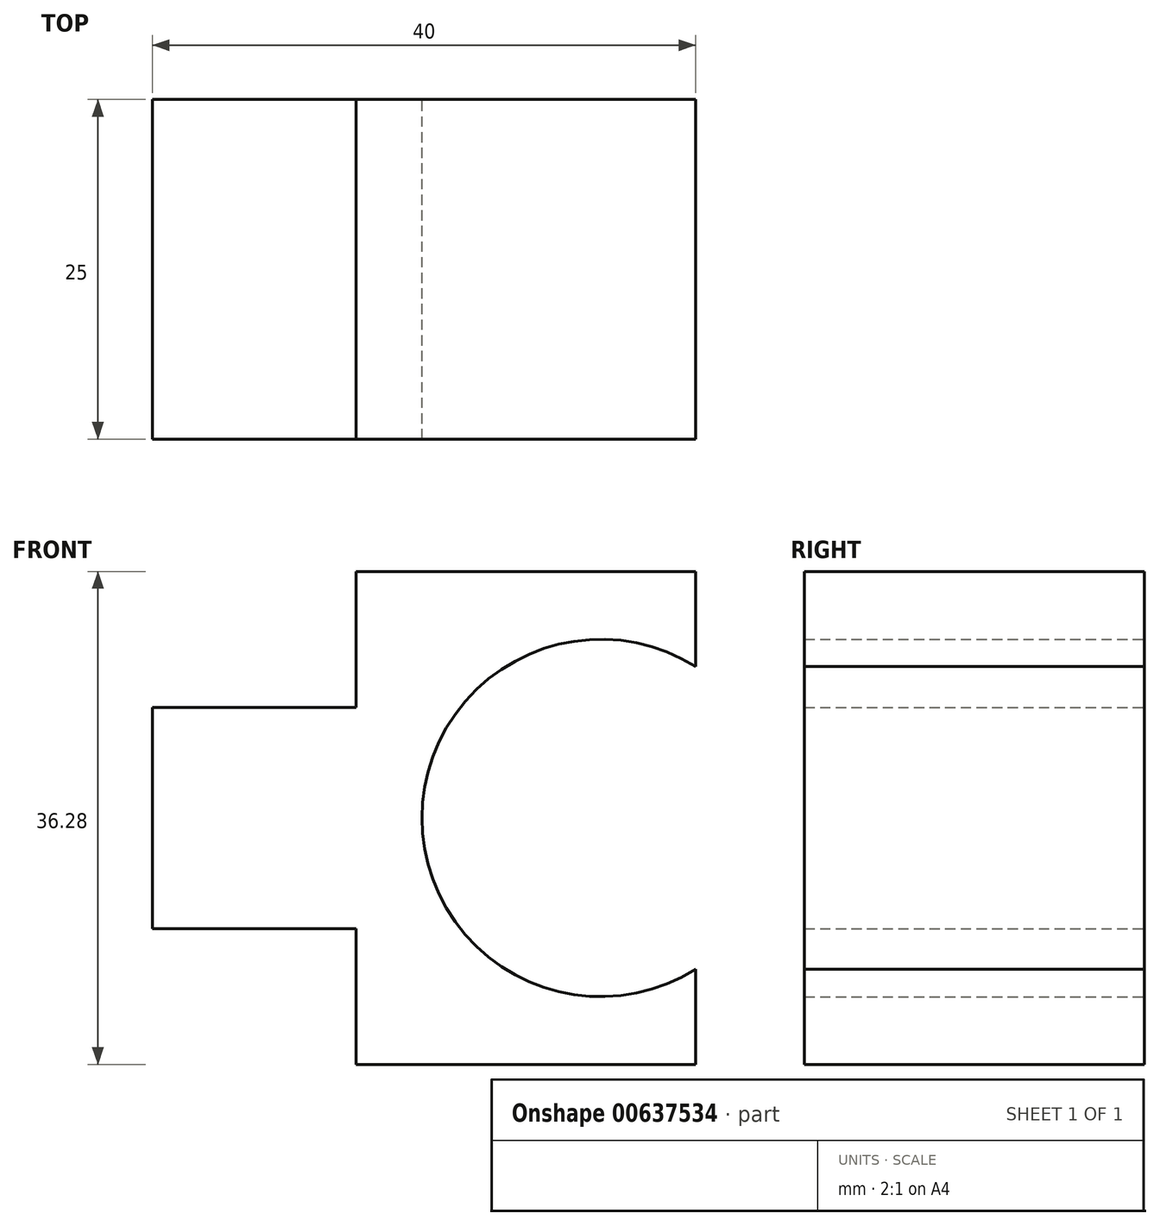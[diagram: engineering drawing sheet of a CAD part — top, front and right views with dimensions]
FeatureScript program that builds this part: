
annotation { "Feature Type Name" : "Feature", "Feature Type Description" : "" }
export const myFeature = defineFeature(function(context is Context, id is Id, definition is map)
    precondition{}
    {
        {
            var Q0;
            Q0=qCreatedBy(makeId("Front.planeOp"),FACE);
            var sketch = newSketch(context, id + "F0", { "sketchPlane" : qUnion([Q0])});
            skLineSegment(sketch, "E0", {"start": v(-25, 36.28) * mm, "end": v(0, 36.28) * mm});
            skLineSegment(sketch, "E1", {"start": v(0, 36.28) * mm, "end": v(0, 29.28) * mm});
            skLineSegment(sketch, "E2", {"start": v(0, 0) * mm, "end": v(-25, 0) * mm});
            skLineSegment(sketch, "E3", {"start": v(-25, 0) * mm, "end": v(-25, 10) * mm});
            skLineSegment(sketch, "E4", {"start": v(-25, 10) * mm, "end": v(-40, 10) * mm});
            skLineSegment(sketch, "E5", {"start": v(-40, 10) * mm, "end": v(-40, 26.28) * mm});
            skLineSegment(sketch, "E6", {"start": v(-40, 26.28) * mm, "end": v(-25, 26.28) * mm});
            skLineSegment(sketch, "E7", {"start": v(-25, 26.28) * mm, "end": v(-25, 36.28) * mm});
            skLineSegment(sketch, "E8", {"start": v(0, 0) * mm, "end": v(0, 7) * mm});
            skArc(sketch, "E9", {"start": v(0, 29.28) * mm, "mid": v(-20.15, 18.14) * mm, "end": v(0, 7) * mm});
            skSolve(sketch);
        }
        {
            var Q0;
            Q0 = qSketchRegion(id + "F0", true);
            extrude(context, id + "F1", {"entities" : qUnion([Q0]), "depth" : 25 * mm, "offsetDistance" : 25 * mm});
        }
    });
